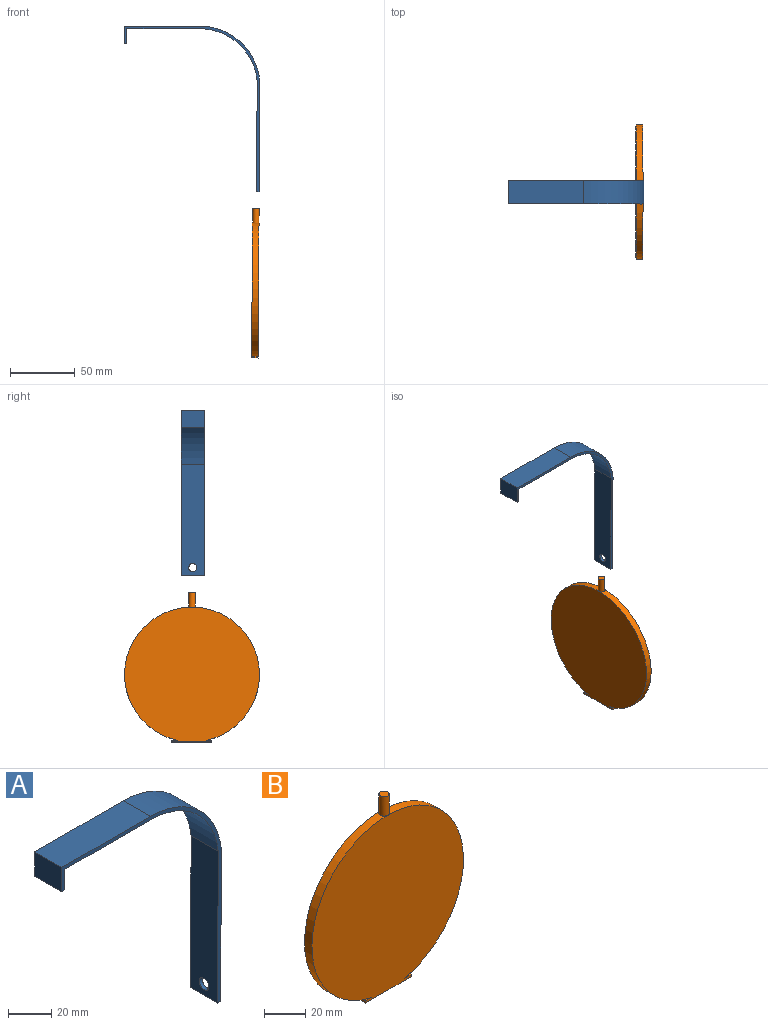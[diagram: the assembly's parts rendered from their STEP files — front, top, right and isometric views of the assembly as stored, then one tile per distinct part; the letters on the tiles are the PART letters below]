
ASSEMBLY  parts=2 mates=2
PART A: 13 faces, bbox 104.7x17.8x128 mm
  f0: plane 17.78x2.03mm, normal (-0.01,0,-1), area 36.1mm2, adj f2,f3,f8,f10
  f1: plane 17.78x2.03mm, normal (0,0,-1), area 36.1mm2, adj f8,f9,f10,f11
  f2: plane 85.79x17.78mm, normal (-1,0,0.01), area 1493.7mm2, adj f0,f6,f8,f10,f12
  f3: plane 85.9x17.78mm, normal (1,0,-0.01), area 1495.6mm2, adj f0,f7,f8,f10,f12
  f4: plane 56.13x17.78mm, normal (0,0,-1), area 998.1mm2, adj f6,f8,f10,f11
  f5: plane 58.17x17.78mm, normal (0,0,1), area 1034.2mm2, adj f7,f8,f9,f10
  f6: cylinder r=44.71mm len=44.48mm, axis (0,1,0), area 1168.1mm2, adj f2,f4,f8,f10
  f7: bspline ~46.53x42.27mm, area 1223.1mm2, adj f3,f5,f8,f10
  f8: plane 128.03x104.68mm, normal (0,-1,0), area 453.1mm2, adj f0,f1,f2,f3,f4,f5,f6,f7
  f9: plane 17.78x13.72mm, normal (-1,0,0), area 243.9mm2, adj f1,f5,f8,f10
  f10: plane 128.03x104.69mm, normal (0,1,0), area 452.7mm2, adj f0,f1,f2,f3,f4,f5,f6,f7
  f11: plane 17.78x11.68mm, normal (1,0,0), area 207.7mm2, adj f1,f4,f8,f10
  f12: cylinder r=3.17mm len=6.36mm, axis (1,0,-0.01), area 40.5mm2, adj f2,f3
PART B: 10 faces, bbox 104.1x5.1x115.6 mm
  f0: cylinder r=52.07mm len=104.14mm, axis (0,1,0), area 1525.5mm2, adj f1,f2,f3,f6,f7
  f1: plane 104.14x104.14mm, normal (0,-1,0), area 8538.2mm2, adj f0,f5,f6,f7,f8,f9
  f2: plane 104.14x104.14mm, normal (0,1,0), area 8538.2mm2, adj f0,f5,f6,f7,f8,f9
  f3: cylinder r=2.48mm len=11.49mm, axis (0,0,-1), area 178.7mm2, adj f0,f4
  f4: plane 4.96x4.96mm, normal (0,0,1), area 19.4mm2, adj f3
  f5: plane 31.37x5.08mm, normal (0,0,-1), area 159.4mm2, adj f1,f2,f8,f9
  f6: plane 5.08x4.72mm, normal (0,0,1), area 24mm2, adj f0,f1,f2,f8
  f7: plane 5.08x3.79mm, normal (0,0,1), area 19.2mm2, adj f0,f1,f2,f9
  f8: plane 5.08x1.27mm, normal (1,0,0), area 6.5mm2, adj f1,f2,f5,f6
  f9: plane 5.08x1.27mm, normal (-1,0,0), area 6.5mm2, adj f1,f2,f5,f7
PLACE A at identity fixed
PLACE B rot(axis=(0,0,1),90deg) t=(97.69,0.64,-190.48)mm
MATE planar A.f3 <-> B.f1  axis (1,0,-0.01) through (103.43,8.89,-71.36)mm
MATE planar A.f0 <-> B.f3  axis (-0.01,0,-1) through (102.17,0,-114.3)mm
